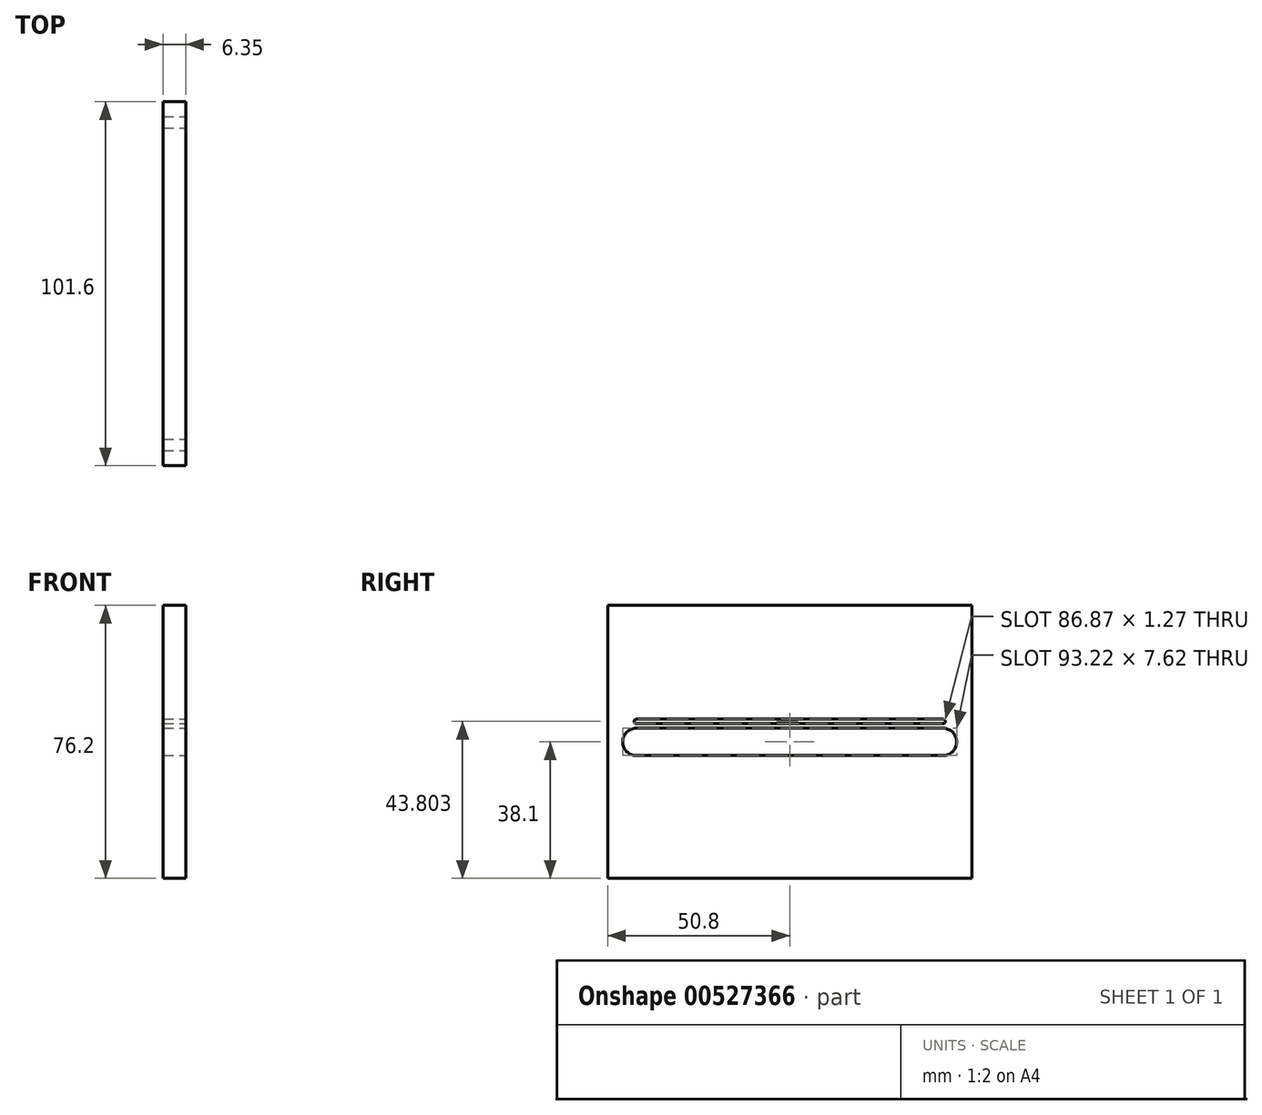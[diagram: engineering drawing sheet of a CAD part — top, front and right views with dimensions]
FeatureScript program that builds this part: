
annotation { "Feature Type Name" : "Feature", "Feature Type Description" : "" }
export const myFeature = defineFeature(function(context is Context, id is Id, definition is map)
    precondition{}
    {
        {
            var Q0;
            Q0=qCreatedBy(makeId("Right.planeOp"),FACE);
            var sketch = newSketch(context, id + "F0", { "sketchPlane" : qUnion([Q0])});
            skLineSegment(sketch, "E0.bottom", {"start": v(50.8, 38.1) * mm, "end": v(-50.8, 38.1) * mm});
            skLineSegment(sketch, "E0.top", {"start": v(50.8, -38.1) * mm, "end": v(-50.8, -38.1) * mm});
            skLineSegment(sketch, "E0.left", {"start": v(50.8, 38.1) * mm, "end": v(50.8, -38.1) * mm});
            skLineSegment(sketch, "E0.right", {"start": v(-50.8, 38.1) * mm, "end": v(-50.8, -38.1) * mm});
            skPoint(sketch, "E0.middle", {"position": v(0, 0) * mm});
            skSolve(sketch);
        }
        {
            var Q0;
            Q0=makeQuery(id+"F0.imprint","IMPRINT",FACE,{"disambiguationData":[TD([[makeQuery(id+"F0.imprint","IMPRINT",EDGE,{"derivedFrom":sQuery(id+"F0.wireOp",EDGE,"E0.bottom")}),1.0]])]});
            extrude(context, id + "F1", {"entities" : qUnion([Q0]), "depth" : 6.35 * mm, "offsetDistance" : 25.4 * mm});
        }
        {
            var Q0;
            Q0=makeQuery(id+"F1.opExtrude","CAP_FACE",FACE,{"disambiguationData":[OSD([sQuery(id+"F0.wireOp",EDGE,"E0.bottom"),sQuery(id+"F0.wireOp",EDGE,"E0.top"),sQuery(id+"F0.wireOp",EDGE,"E0.left"),sQuery(id+"F0.wireOp",EDGE,"E0.right")])],"isStart":false});
            var sketch = newSketch(context, id + "F2", { "sketchPlane" : qUnion([Q0])});
            skArc(sketch, "E1", {"start": v(-42.8, 3.81) * mm, "mid": v(-46.6, 0) * mm, "end": v(-42.8, -3.81) * mm});
            skArc(sketch, "E2", {"start": v(42.8, -3.81) * mm, "mid": v(46.6, 0) * mm, "end": v(42.8, 3.81) * mm});
            skLineSegment(sketch, "E3", {"start": v(-42.8, 3.81) * mm, "end": v(42.8, 3.81) * mm});
            skLineSegment(sketch, "E4", {"start": v(-42.8, -3.81) * mm, "end": v(42.8, -3.81) * mm});
            skSolve(sketch);
        }
        {
            var Q0;
            Q0 = qSketchRegion(id + "F2", true);
            extrude(context, id + "F3", {"entities" : qUnion([Q0]), "operationType" : NewBodyOperationType.REMOVE, "oppositeDirection" : true, "depth" : 25.4 * mm, "offsetDistance" : 25.4 * mm});
        }
        {
            var Q0;
            Q0=makeQuery(id+"F1.opExtrude","CAP_FACE",FACE,{"disambiguationData":[OSD([sQuery(id+"F0.wireOp",EDGE,"E0.bottom"),sQuery(id+"F0.wireOp",EDGE,"E0.top"),sQuery(id+"F0.wireOp",EDGE,"E0.left"),sQuery(id+"F0.wireOp",EDGE,"E0.right")])],"isStart":false});
            var sketch = newSketch(context, id + "F4", { "sketchPlane" : qUnion([Q0])});
            skArc(sketch, "E5", {"start": v(42.8, 5.07) * mm, "mid": v(43.43, 5.7) * mm, "end": v(42.8, 6.34) * mm});
            skArc(sketch, "E6", {"start": v(-42.8, 6.34) * mm, "mid": v(-43.43, 5.7) * mm, "end": v(-42.8, 5.07) * mm});
            skLineSegment(sketch, "E7", {"start": v(-42.8, 5.07) * mm, "end": v(42.8, 5.07) * mm});
            skLineSegment(sketch, "E8", {"start": v(42.8, 6.34) * mm, "end": v(-42.8, 6.34) * mm});
            skSolve(sketch);
        }
        {
            var Q0;
            Q0 = qSketchRegion(id + "F4", true);
            extrude(context, id + "F5", {"entities" : qUnion([Q0]), "operationType" : NewBodyOperationType.REMOVE, "oppositeDirection" : true, "depth" : 25.4 * mm, "offsetDistance" : 25.4 * mm});
        }
    });
